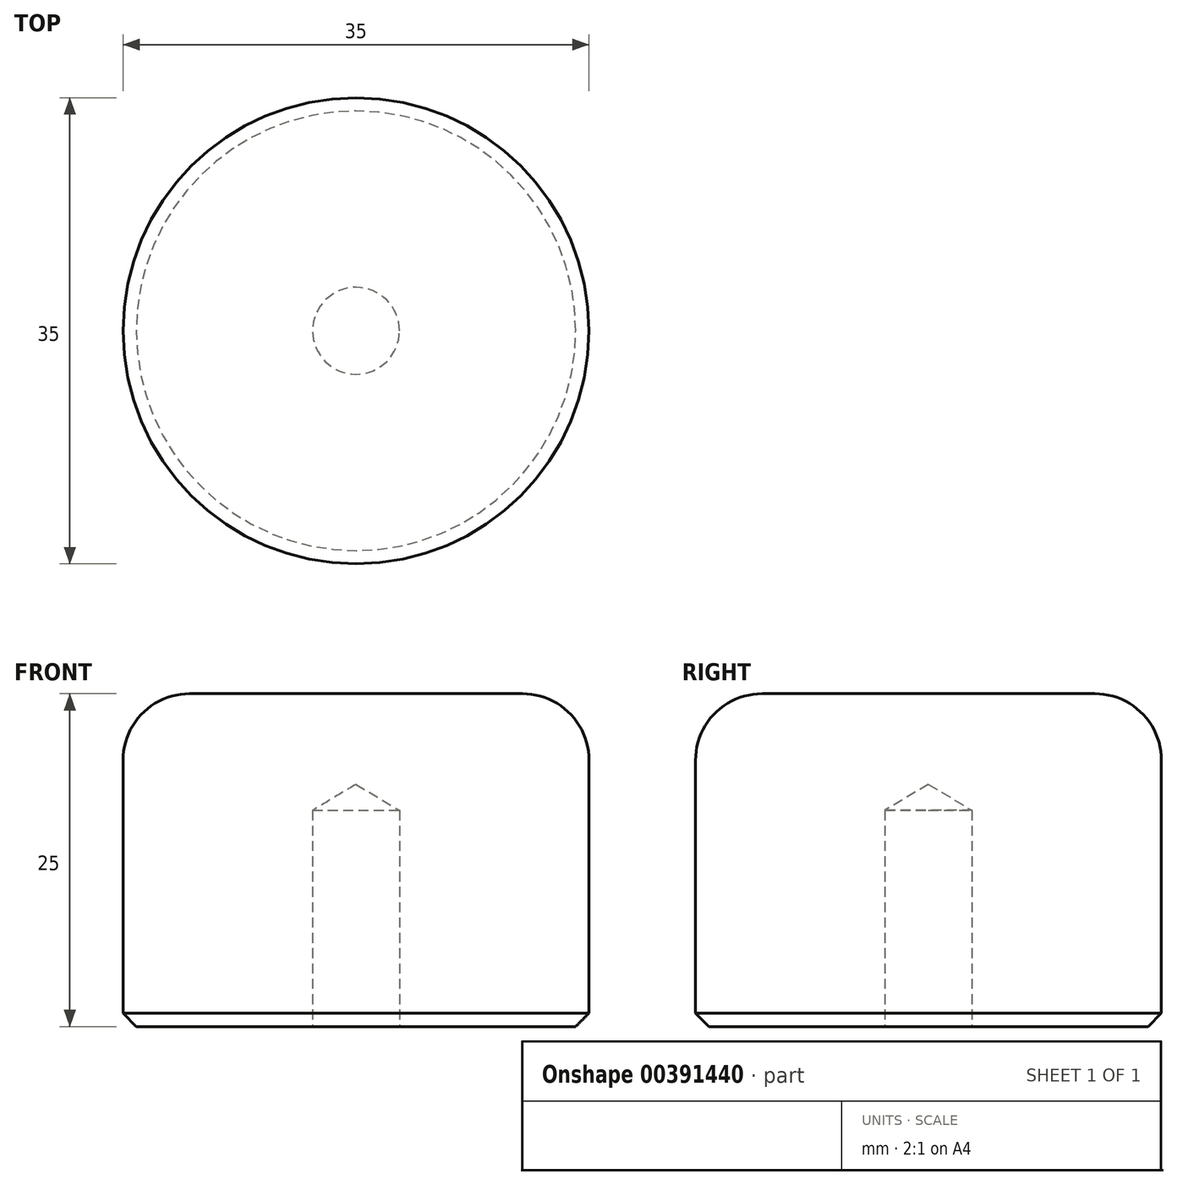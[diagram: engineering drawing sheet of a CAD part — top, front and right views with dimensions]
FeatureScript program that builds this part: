
annotation { "Feature Type Name" : "Feature", "Feature Type Description" : "" }
export const myFeature = defineFeature(function(context is Context, id is Id, definition is map)
    precondition{}
    {
        {
            var Q0;
            Q0=qCreatedBy(makeId("Top.planeOp"),FACE);
            var sketch = newSketch(context, id + "F0", { "sketchPlane" : qUnion([Q0])});
            skCircle(sketch, "E0", {"center": v(0, 0) * mm, "radius": 17.5 * mm});
            skSolve(sketch);
        }
        {
            var Q0;
            Q0=qSketchRegion(id+"F0",true);
            extrude(context, id + "F1", {"entities" : qUnion([Q0]), "depth" : 25 * mm});
        }
        {
            var Q0;
            Q0=makeQuery(id+"F1.opExtrude","CAP_EDGE",EDGE,{"disambiguationData":[OSD([sQuery(id+"F0.wireOp",EDGE,"E0")])],"isStart":false});
            fillet(context, id + "F2", {"entities" : qUnion([Q0]), "radius" : 5 * mm, "tangentPropagation" : true, "allowEdgeOverflow" : false});
        }
        {
            var Q0;
            Q0=makeQuery(id+"F1.opExtrude","CAP_EDGE",EDGE,{"disambiguationData":[OSD([sQuery(id+"F0.wireOp",EDGE,"E0")])],"isStart":true});
            chamfer(context, id + "F3", {"entities" : qUnion([Q0]), "width" : 1 * mm, "tangentPropagation" : true});
        }
        {
            var Q0;
            Q0=sQuery(id+"F0.wireOp",VERTEX,"E0.center");
            var Q1;
            Q1=makeQuery(id+"F1.opExtrude","SWEPT_BODY",BODY,{"disambiguationData":[OSD([sQuery(id+"F0.wireOp",EDGE,"E0")])]});
            hole(context, id + "F4", {"style" : HoleStyle.SIMPLE, "endStyle" : HoleEndStyle.BLIND, "oppositeDirection" : true, "standardTappedOrClearance" : lookupTablePath({ "standard" : "ANSI", "engagement" : "75%", "pitch" : "18 tpi", "size" : "5/16", "type" : "Tapped" }), "standardBlindInLast" : lookupTablePath({ "standard" : "ANSI", "engagement" : "75%", "pitch" : "18 tpi", "size" : "5/16", "type" : "Tapped" }), "holeDiameter" : 6.53 * mm, "showTappedDepth" : true, "holeDepth" : 16.23 * mm, "tappedDepth" : 12 * mm, "tapClearance" : 3, "startFromSketch" : true, "locations" : qUnion([Q0]), "scope" : qUnion([Q1]), "majorDiameter" : 7.94 * mm});
        }
    });
